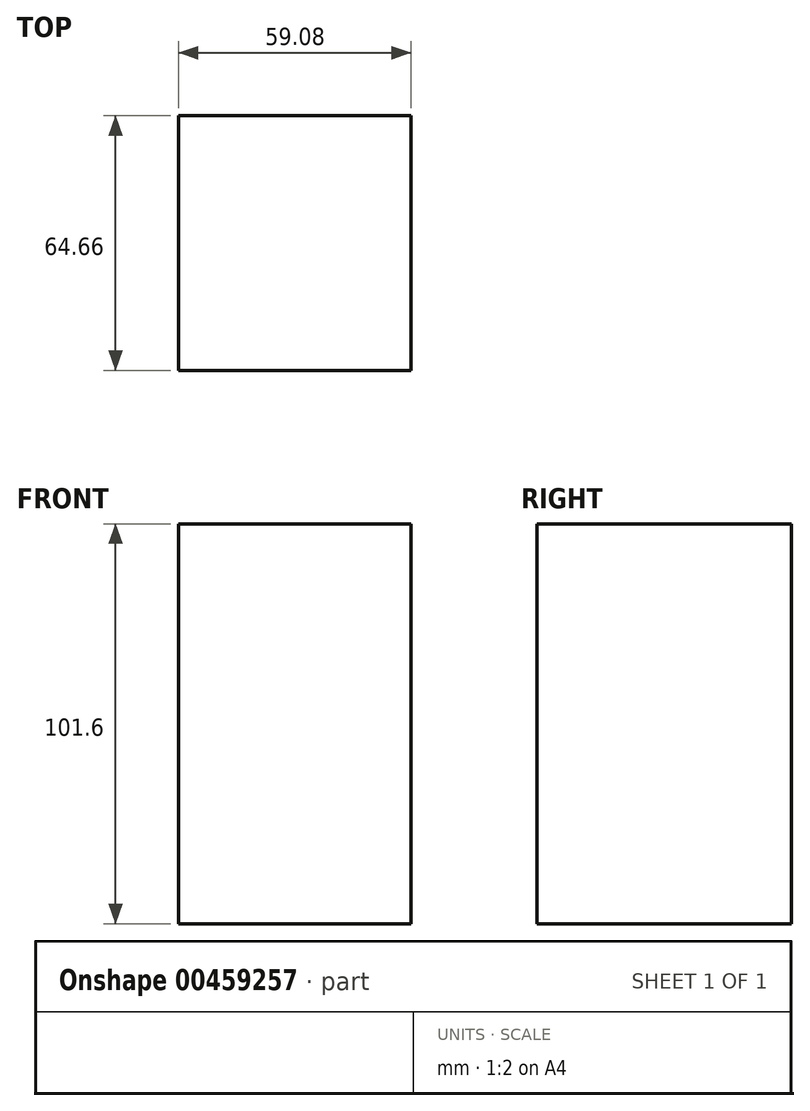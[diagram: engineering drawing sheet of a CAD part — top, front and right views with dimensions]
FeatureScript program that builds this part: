
annotation { "Feature Type Name" : "Feature", "Feature Type Description" : "" }
export const myFeature = defineFeature(function(context is Context, id is Id, definition is map)
    precondition{}
    {
        {
            var Q0;
            Q0=qCreatedBy(makeId("Top.planeOp"),FACE);
            var sketch = newSketch(context, id + "F0", { "sketchPlane" : qUnion([Q0])});
            skLineSegment(sketch, "E0.bottom", {"start": v(29.54, 32.33) * mm, "end": v(-29.54, 32.33) * mm});
            skLineSegment(sketch, "E0.top", {"start": v(29.54, -32.33) * mm, "end": v(-29.54, -32.33) * mm});
            skLineSegment(sketch, "E0.left", {"start": v(29.54, 32.33) * mm, "end": v(29.54, -32.33) * mm});
            skLineSegment(sketch, "E0.right", {"start": v(-29.54, 32.33) * mm, "end": v(-29.54, -32.33) * mm});
            skPoint(sketch, "E0.middle", {"position": v(0, 0) * mm});
            skSolve(sketch);
        }
        {
            var Q0;
            Q0=makeQuery(id+"F0.imprint","IMPRINT",FACE,{"disambiguationData":[TD([[makeQuery(id+"F0.imprint","IMPRINT",EDGE,{"derivedFrom":sQuery(id+"F0.wireOp",EDGE,"E0.bottom")}),1.0]])]});
            extrude(context, id + "F1", {"entities" : qUnion([Q0]), "depth" : 101.6 * mm});
        }
    });
